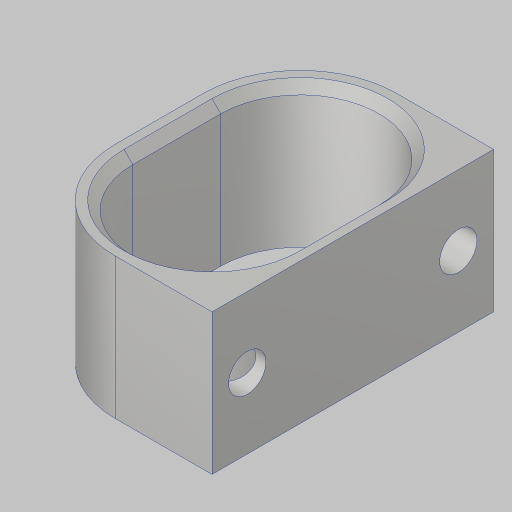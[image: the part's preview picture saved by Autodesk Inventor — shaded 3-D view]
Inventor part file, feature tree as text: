
AUTODESK INVENTOR PART (.ipt)
format: ipt  version: 2023.5 (Build 275446000, 446)  size: 171,008 bytes
history: native  units: in
note: dims shown in document units (in); Inventor stores cm internally (conversion verified against a paired STEP export)
features: extrude x3, projected_geometry x3, sketch x2, chamfer x1
ambient origin geometry x8: Origin, YZ Plane, XZ Plane, XY Plane, X Axis, Y Axis, Z Axis, Center Point
bodies: Solid1 (feature_tree)
feature tree (9):
  sketch  "Sketch1"  dims[d1=1.375in d2=0.125in]
  extrude  "Extrusion1"  Depth=0.125in
  extrude  "Extrusion2"  Depth=1.0in TaperAngle=0.0deg
  extrude  "Extrusion3"  Depth=0.125in
  chamfer  "Chamfer1"  Distance=1.5in
  sketch  "Sketch2"  dims[d3=2.0in d4=1.0in d5=0.0in d6=0.2657in d7=1.5in d8=1.0in d9=0.0in d10=1.0in d11=0.0in d12=0.0625in d13=0.125in d14=45.0deg]
  projected_geometry  "Projected Loop1"
  projected_geometry  "Projected Loop2"
  projected_geometry  "Projected Loop3"
